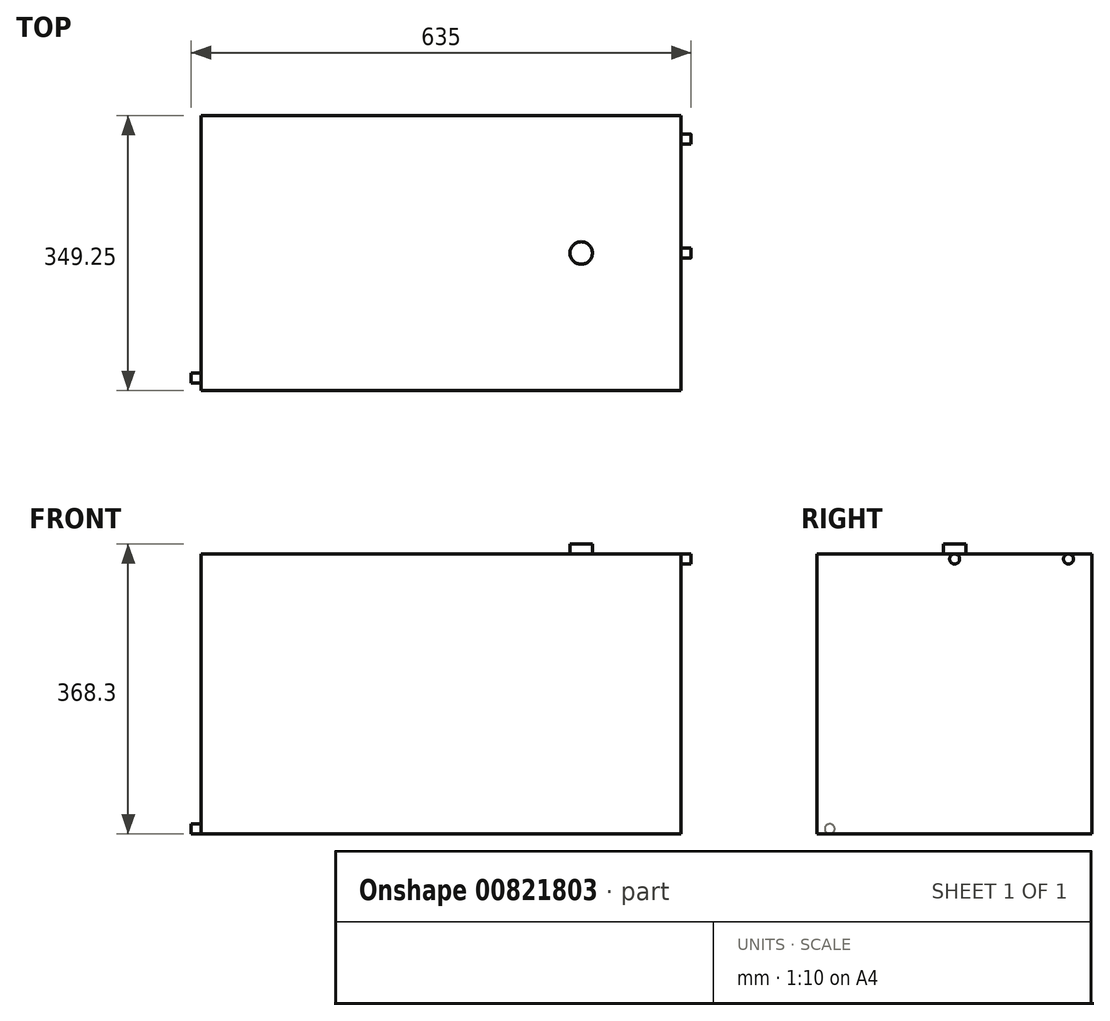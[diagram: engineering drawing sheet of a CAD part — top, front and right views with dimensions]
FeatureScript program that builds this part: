
annotation { "Feature Type Name" : "Feature", "Feature Type Description" : "" }
export const myFeature = defineFeature(function(context is Context, id is Id, definition is map)
    precondition{}
    {
        {
            var Q0;
            Q0=qCreatedBy(makeId("Top.planeOp"),FACE);
            var sketch = newSketch(context, id + "F0", { "sketchPlane" : qUnion([Q0])});
            skLineSegment(sketch, "E0", {"start": v(0, 0) * mm, "end": v(0, 349.25) * mm});
            skLineSegment(sketch, "E1", {"start": v(0, 0) * mm, "end": v(-609.6, 0) * mm});
            skLineSegment(sketch, "E2", {"start": v(-609.6, 0) * mm, "end": v(-609.6, 349.25) * mm});
            skLineSegment(sketch, "E3", {"start": v(-609.6, 349.25) * mm, "end": v(0, 349.25) * mm});
            skSolve(sketch);
        }
        {
            var Q0;
            Q0 = qSketchRegion(id + "F0", true);
            extrude(context, id + "F1", {"entities" : qUnion([Q0]), "depth" : 355.6 * mm, "offsetDistance" : 25.4 * mm});
        }
        {
            var Q0;
            Q0=makeQuery(id+"F1.opExtrude","CAP_FACE",FACE,{"disambiguationData":[OSD([sQuery(id+"F0.wireOp",EDGE,"E0"),sQuery(id+"F0.wireOp",EDGE,"E1"),sQuery(id+"F0.wireOp",EDGE,"E2"),sQuery(id+"F0.wireOp",EDGE,"E3")])],"isStart":false});
            var sketch = newSketch(context, id + "F2", { "sketchPlane" : qUnion([Q0])});
            skLineSegment(sketch, "E4", {"start": v(-304.8, 349.25) * mm, "end": v(-304.8, 0) * mm});
            skLineSegment(sketch, "E5", {"start": v(-304.8, 174.63) * mm, "end": v(-127, 174.63) * mm});
            skCircle(sketch, "E6", {"center": v(-127, 174.63) * mm, "radius": 14.29 * mm});
            skSolve(sketch);
        }
        {
            var Q0;
            Q0 = qSketchRegion(id + "F2", true);
            extrude(context, id + "F3", {"entities" : qUnion([Q0]), "operationType" : NewBodyOperationType.ADD, "depth" : 12.7 * mm, "offsetDistance" : 25.4 * mm});
        }
        {
            var Q0;
            Q0=makeQuery(id+"F1.opExtrude","SWEPT_FACE",FACE,{"disambiguationData":[OSD([sQuery(id+"F0.wireOp",EDGE,"E0")])]});
            var sketch = newSketch(context, id + "F4", { "sketchPlane" : qUnion([Q0])});
            skCircle(sketch, "E7", {"center": v(174.63, 349.25) * mm, "radius": 6.35 * mm});
            skPoint(sketch, "E7.centerSnap0", {"position": v(174.63, 355.6) * mm});
            skCircle(sketch, "E8", {"center": v(319.28, 349.25) * mm, "radius": 6.35 * mm});
            skSolve(sketch);
        }
        {
            var Q0;
            Q0 = qSketchRegion(id + "F4", true);
            extrude(context, id + "F5", {"entities" : qUnion([Q0]), "operationType" : NewBodyOperationType.ADD, "depth" : 12.7 * mm, "offsetDistance" : 25.4 * mm});
        }
        {
            var Q0;
            Q0=makeQuery(id+"F1.opExtrude","SWEPT_FACE",FACE,{"disambiguationData":[OSD([sQuery(id+"F0.wireOp",EDGE,"E2")])]});
            var sketch = newSketch(context, id + "F6", { "sketchPlane" : qUnion([Q0])});
            skCircle(sketch, "E9", {"center": v(-15.96, 6.35) * mm, "radius": 6.35 * mm});
            skSolve(sketch);
        }
        {
            var Q0;
            Q0 = qSketchRegion(id + "F6", true);
            extrude(context, id + "F7", {"entities" : qUnion([Q0]), "operationType" : NewBodyOperationType.ADD, "depth" : 12.7 * mm, "offsetDistance" : 25.4 * mm});
        }
    });
